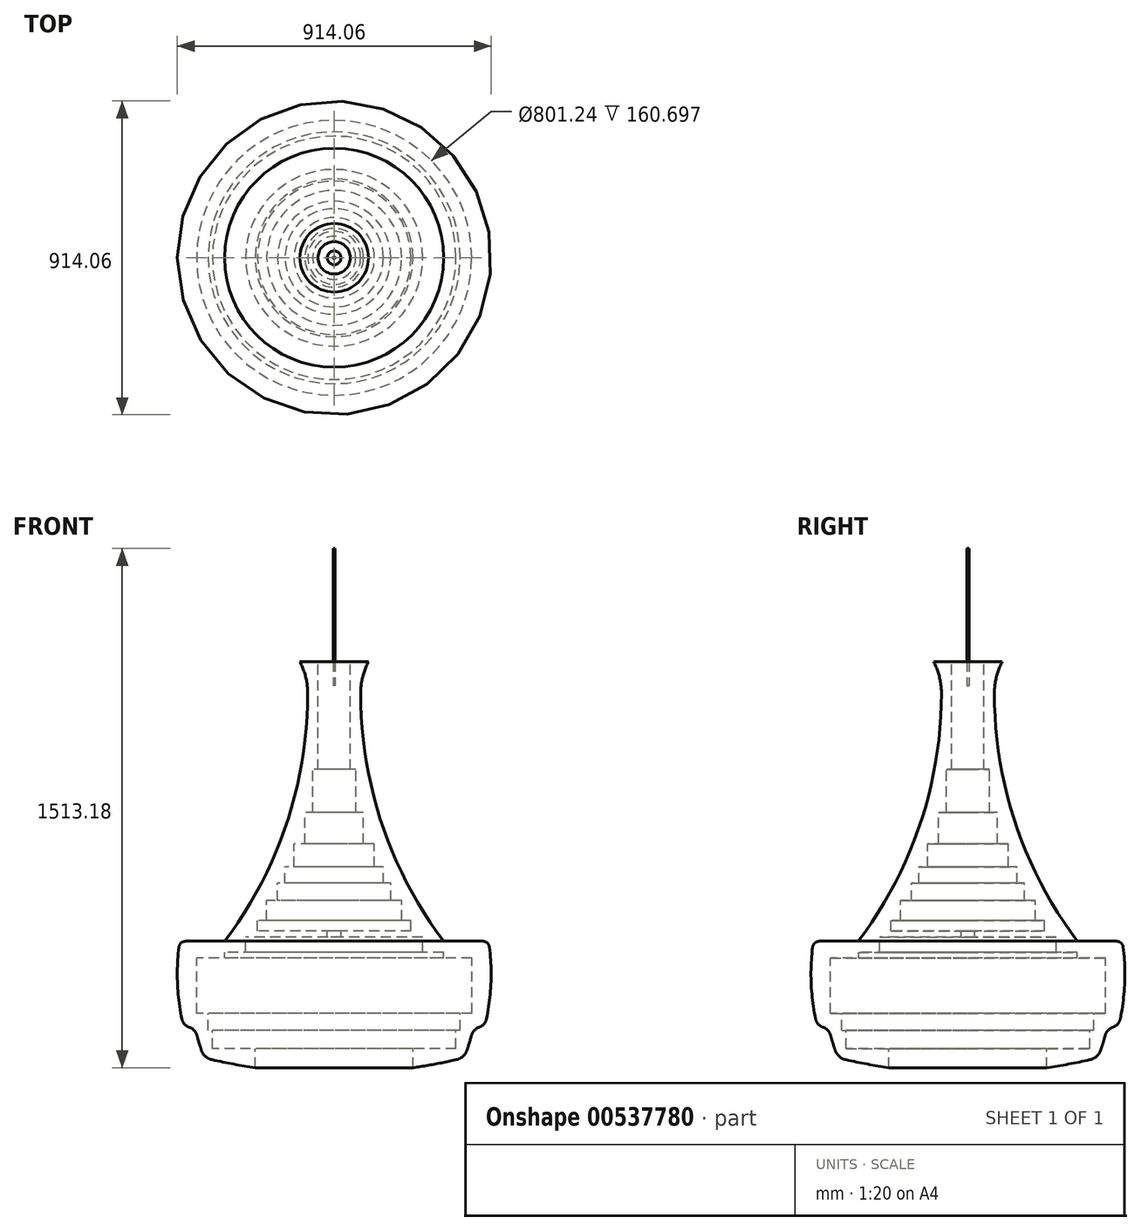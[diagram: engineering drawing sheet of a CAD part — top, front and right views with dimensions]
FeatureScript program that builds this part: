
annotation { "Feature Type Name" : "Feature", "Feature Type Description" : "" }
export const myFeature = defineFeature(function(context is Context, id is Id, definition is map)
    precondition{}
    {
        {
            var Q0;
            Q0=qCreatedBy(makeId("Front.planeOp"),FACE);
            var sketch = newSketch(context, id + "F0", { "sketchPlane" : qUnion([Q0])});
            skArc(sketch, "E0", {"start": v(-318.85, 205.39) * mm, "mid": v(-139.14, 546.86) * mm, "end": v(-77.1, 927.71) * mm});
            skLineSegment(sketch, "E1", {"start": v(-318.85, 205.39) * mm, "end": v(-450, 205.39) * mm});
            skArc(sketch, "E2", {"start": v(-450, 205.39) * mm, "mid": v(-456.78, 91.82) * mm, "end": v(-443.64, -21.2) * mm});
            skArc(sketch, "E3", {"start": v(-355.53, -140.06) * mm, "mid": v(-293, -152.86) * mm, "end": v(-230, -163.18) * mm});
            skArc(sketch, "E4", {"start": v(-77.1, 927.71) * mm, "mid": v(-82.9, 975.45) * mm, "end": v(-100, 1020.39) * mm});
            skArc(sketch, "E5", {"start": v(-443.64, -21.2) * mm, "mid": v(-436.32, -35.87) * mm, "end": v(-422.68, -44.97) * mm});
            skArc(sketch, "E6", {"start": v(-422.68, -44.97) * mm, "mid": v(-408.12, -54.37) * mm, "end": v(-399.7, -69.52) * mm});
            skArc(sketch, "E7", {"start": v(-399.7, -69.52) * mm, "mid": v(-393.61, -90.8) * mm, "end": v(-386.84, -111.88) * mm});
            skArc(sketch, "E8", {"start": v(-386.84, -111.88) * mm, "mid": v(-374.87, -130.06) * mm, "end": v(-355.53, -140.06) * mm});
            skLineSegment(sketch, "E9.2", {"start": v(-318.34, 156.2) * mm, "end": v(-400.62, 156.2) * mm});
            skLineSegment(sketch, "E10", {"start": v(-77.1, 927.71) * mm, "end": v(-77.1, 1090.53) * mm, "construction": true});
            skLineSegment(sketch, "E11", {"start": v(-100, 1020.39) * mm, "end": v(-47.12, 1020.39) * mm});
            skLineSegment(sketch, "E12", {"start": v(-47.12, 1020.39) * mm, "end": v(-47.12, 705.76) * mm});
            skLineSegment(sketch, "E13", {"start": v(-47.12, 705.76) * mm, "end": v(-62.96, 705.76) * mm});
            skLineSegment(sketch, "E14", {"start": v(-62.96, 705.76) * mm, "end": v(-62.96, 580.2) * mm});
            skLineSegment(sketch, "E15", {"start": v(-62.96, 580.2) * mm, "end": v(-85.58, 580.2) * mm});
            skLineSegment(sketch, "E16", {"start": v(-85.58, 580.2) * mm, "end": v(-85.58, 489.7) * mm});
            skLineSegment(sketch, "E17", {"start": v(-85.58, 489.7) * mm, "end": v(-117.26, 489.7) * mm});
            skLineSegment(sketch, "E18", {"start": v(-117.26, 489.7) * mm, "end": v(-117.26, 421.82) * mm});
            skLineSegment(sketch, "E19", {"start": v(-117.26, 421.82) * mm, "end": v(-143.28, 421.82) * mm});
            skLineSegment(sketch, "E20", {"start": v(-143.28, 421.82) * mm, "end": v(-143.28, 374.3) * mm});
            skLineSegment(sketch, "E21", {"start": v(-143.28, 374.3) * mm, "end": v(-164.77, 374.3) * mm});
            skLineSegment(sketch, "E22", {"start": v(-164.77, 374.3) * mm, "end": v(-164.77, 323.4) * mm});
            skLineSegment(sketch, "E23", {"start": v(-164.77, 323.4) * mm, "end": v(-196.45, 323.4) * mm});
            skLineSegment(sketch, "E24", {"start": v(-196.45, 323.4) * mm, "end": v(-196.45, 265.7) * mm});
            skLineSegment(sketch, "E25", {"start": v(-196.45, 265.7) * mm, "end": v(-223.6, 265.7) * mm});
            skLineSegment(sketch, "E26", {"start": v(-20, 217.5) * mm, "end": v(-257.53, 217.5) * mm});
            skLineSegment(sketch, "E27", {"start": v(-257.53, 217.5) * mm, "end": v(-257.53, 173.02) * mm});
            skLineSegment(sketch, "E28", {"start": v(-257.53, 173.02) * mm, "end": v(-318.34, 173.02) * mm});
            skLineSegment(sketch, "E29", {"start": v(-318.34, 173.02) * mm, "end": v(-318.34, 156.2) * mm});
            skLineSegment(sketch, "E30", {"start": v(-400.62, 156.2) * mm, "end": v(-400.62, -4.5) * mm});
            skLineSegment(sketch, "E31", {"start": v(-400.62, -4.5) * mm, "end": v(-366.89, -4.5) * mm});
            skLineSegment(sketch, "E32", {"start": v(-366.89, -4.5) * mm, "end": v(-366.89, -54.5) * mm});
            skLineSegment(sketch, "E33", {"start": v(-366.89, -54.5) * mm, "end": v(-354.62, -54.5) * mm});
            skLineSegment(sketch, "E34", {"start": v(-354.62, -54.5) * mm, "end": v(-354.62, -107.23) * mm});
            skLineSegment(sketch, "E35", {"start": v(-354.62, -107.23) * mm, "end": v(-230, -107.23) * mm});
            skLineSegment(sketch, "E36", {"start": v(-230, -107.23) * mm, "end": v(-230, -163.18) * mm});
            skPoint(sketch, "E37.start.orphan", {"position": v(0, -179.61) * mm});
            skLineSegment(sketch, "E38", {"start": v(0, 61.45) * mm, "end": v(0, -58.83) * mm, "construction": true});
            skLineSegment(sketch, "E39", {"start": v(-223.6, 265.7) * mm, "end": v(-223.6, 235.5) * mm});
            skLineSegment(sketch, "E40", {"start": v(-223.6, 235.5) * mm, "end": v(-20, 235.5) * mm});
            skLineSegment(sketch, "E41", {"start": v(-20, 235.5) * mm, "end": v(-20, 217.5) * mm});
            skSolve(sketch);
        }
        {
            var Q0;
            Q0=makeQuery(id+"F0.imprint","IMPRINT",FACE,{"disambiguationData":[TD([[makeQuery(id+"F0.imprint","IMPRINT",EDGE,{"derivedFrom":sQuery(id+"F0.wireOp",EDGE,"E0")}),-1.0]])]});
            var Q1;
            Q1=sQuery(id+"F0.wireOp",EDGE,"E38");
            revolve(context, id + "F1", {"entities" : qUnion([Q0]), "axis" : qUnion([Q1]), "revolveType" : RevolveType.FULL});
        }
        {
            var Q0;
            Q0=qCreatedBy(makeId("Top.planeOp"),FACE);
            cPlane(context, id + "F2", {"entities" : qUnion([Q0]), "cplaneType" : CPlaneType.OFFSET, "offset" : 950 * mm, "width" : 150 * mm, "height" : 150 * mm});
        }
        {
            var Q0;
            Q0=qCreatedBy(id+"F2.planeOp",FACE);
            var sketch = newSketch(context, id + "F3", { "sketchPlane" : qUnion([Q0])});
            skCircle(sketch, "E42", {"center": v(0, 0) * mm, "radius": 3 * mm});
            skSolve(sketch);
        }
        {
            var Q0;
            Q0 = qSketchRegion(id + "F3", true);
            extrude(context, id + "F4", {"entities" : qUnion([Q0]), "depth" : 400 * mm, "offsetDistance" : 25 * mm});
        }
        {
            var Q0;
            Q0=makeQuery(id+"F1.opRevolve","SWEPT_EDGE",EDGE,{"disambiguationData":[OSD([sQuery(id+"F0.wireOp",EDGE,"E1"),sQuery(id+"F0.wireOp",EDGE,"E2")])]});
            fillet(context, id + "F5", {"entities" : qUnion([Q0]), "radius" : 20 * mm, "tangentPropagation" : true, "allowEdgeOverflow" : false});
        }
    });
